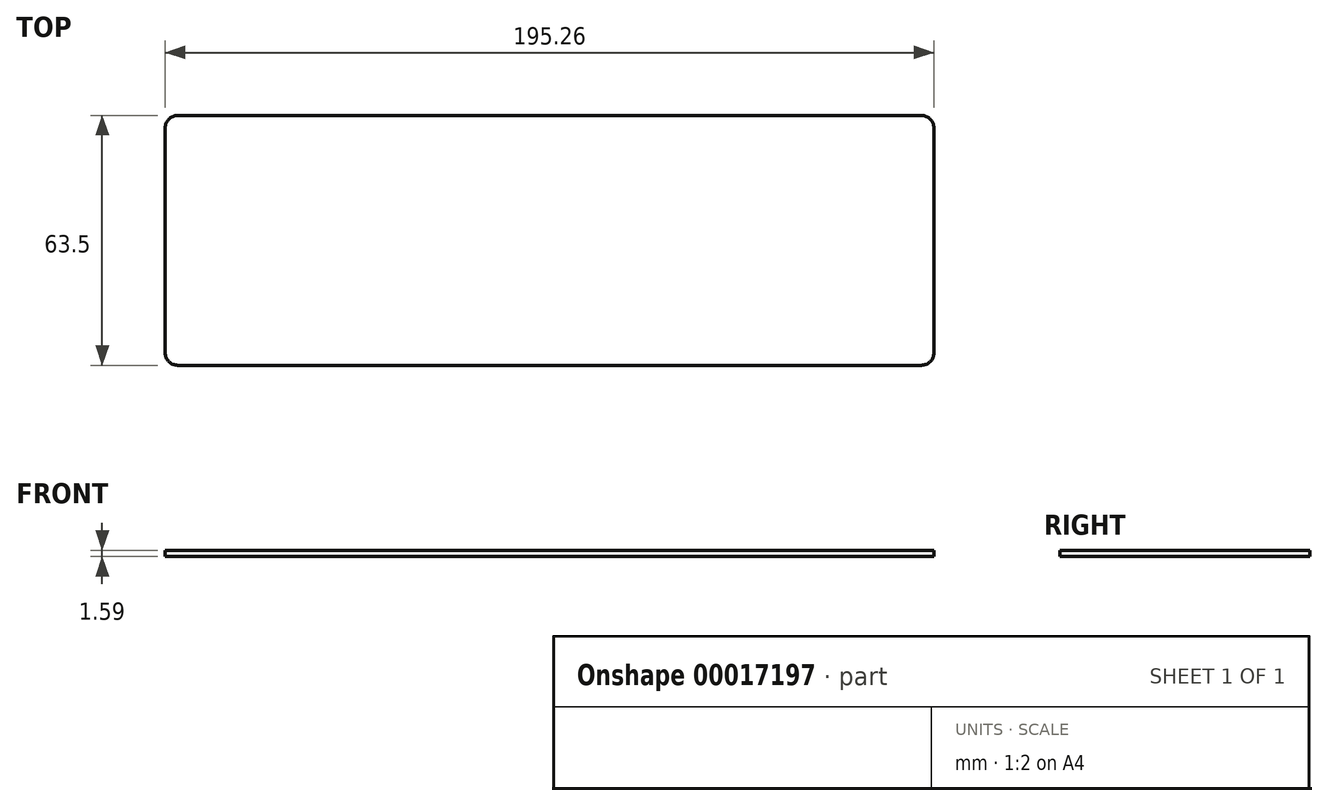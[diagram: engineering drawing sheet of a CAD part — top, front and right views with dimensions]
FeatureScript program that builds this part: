
annotation { "Feature Type Name" : "Feature", "Feature Type Description" : "" }
export const myFeature = defineFeature(function(context is Context, id is Id, definition is map)
    precondition{}
    {
        {
            var Q0;
            Q0=qCreatedBy(makeId("Top.planeOp"),FACE);
            var sketch = newSketch(context, id + "F0", { "sketchPlane" : qUnion([Q0])});
            skLineSegment(sketch, "E0.bottom", {"start": v(0, 0) * mm, "end": v(195.26, 0) * mm});
            skLineSegment(sketch, "E0.top", {"start": v(0, 63.5) * mm, "end": v(195.26, 63.5) * mm});
            skLineSegment(sketch, "E0.left", {"start": v(0, 0) * mm, "end": v(0, 63.5) * mm});
            skLineSegment(sketch, "E0.right", {"start": v(195.26, 0) * mm, "end": v(195.26, 63.5) * mm});
            skSolve(sketch);
        }
        {
            var Q0;
            Q0=makeQuery(id+"F0.imprint","IMPRINT",FACE,{"disambiguationData":[TD([[makeQuery(id+"F0.imprint","IMPRINT",EDGE,{"derivedFrom":sQuery(id+"F0.wireOp",EDGE,"E0.bottom")}),1.0]])]});
            extrude(context, id + "F1", {"entities" : qUnion([Q0]), "depth" : 1.59 * mm});
        }
        {
            var Q0;
            Q0=makeQuery(id+"F1.opExtrude","SWEPT_EDGE",EDGE,{"disambiguationData":[OSD([sQuery(id+"F0.wireOp",EDGE,"E0.top"),sQuery(id+"F0.wireOp",EDGE,"E0.left")])]});
            fillet(context, id + "F2", {"entities" : qUnion([Q0]), "radius" : 3.17 * mm, "allowEdgeOverflow" : false});
        }
        {
            var Q0;
            Q0=makeQuery(id+"F1.opExtrude","SWEPT_EDGE",EDGE,{"disambiguationData":[OSD([sQuery(id+"F0.wireOp",EDGE,"E0.bottom"),sQuery(id+"F0.wireOp",EDGE,"E0.left")])]});
            fillet(context, id + "F3", {"entities" : qUnion([Q0]), "radius" : 3.17 * mm, "tangentPropagation" : true, "allowEdgeOverflow" : false});
        }
        {
            var Q0;
            Q0=makeQuery(id+"F1.opExtrude","SWEPT_EDGE",EDGE,{"disambiguationData":[OSD([sQuery(id+"F0.wireOp",EDGE,"E0.bottom"),sQuery(id+"F0.wireOp",EDGE,"E0.right")])]});
            fillet(context, id + "F4", {"entities" : qUnion([Q0]), "radius" : 3.17 * mm, "tangentPropagation" : true, "allowEdgeOverflow" : false});
        }
        {
            var Q0;
            Q0=makeQuery(id+"F1.opExtrude","SWEPT_EDGE",EDGE,{"disambiguationData":[OSD([sQuery(id+"F0.wireOp",EDGE,"E0.top"),sQuery(id+"F0.wireOp",EDGE,"E0.right")])]});
            fillet(context, id + "F5", {"entities" : qUnion([Q0]), "radius" : 3.17 * mm, "tangentPropagation" : true, "allowEdgeOverflow" : false});
        }
    });
